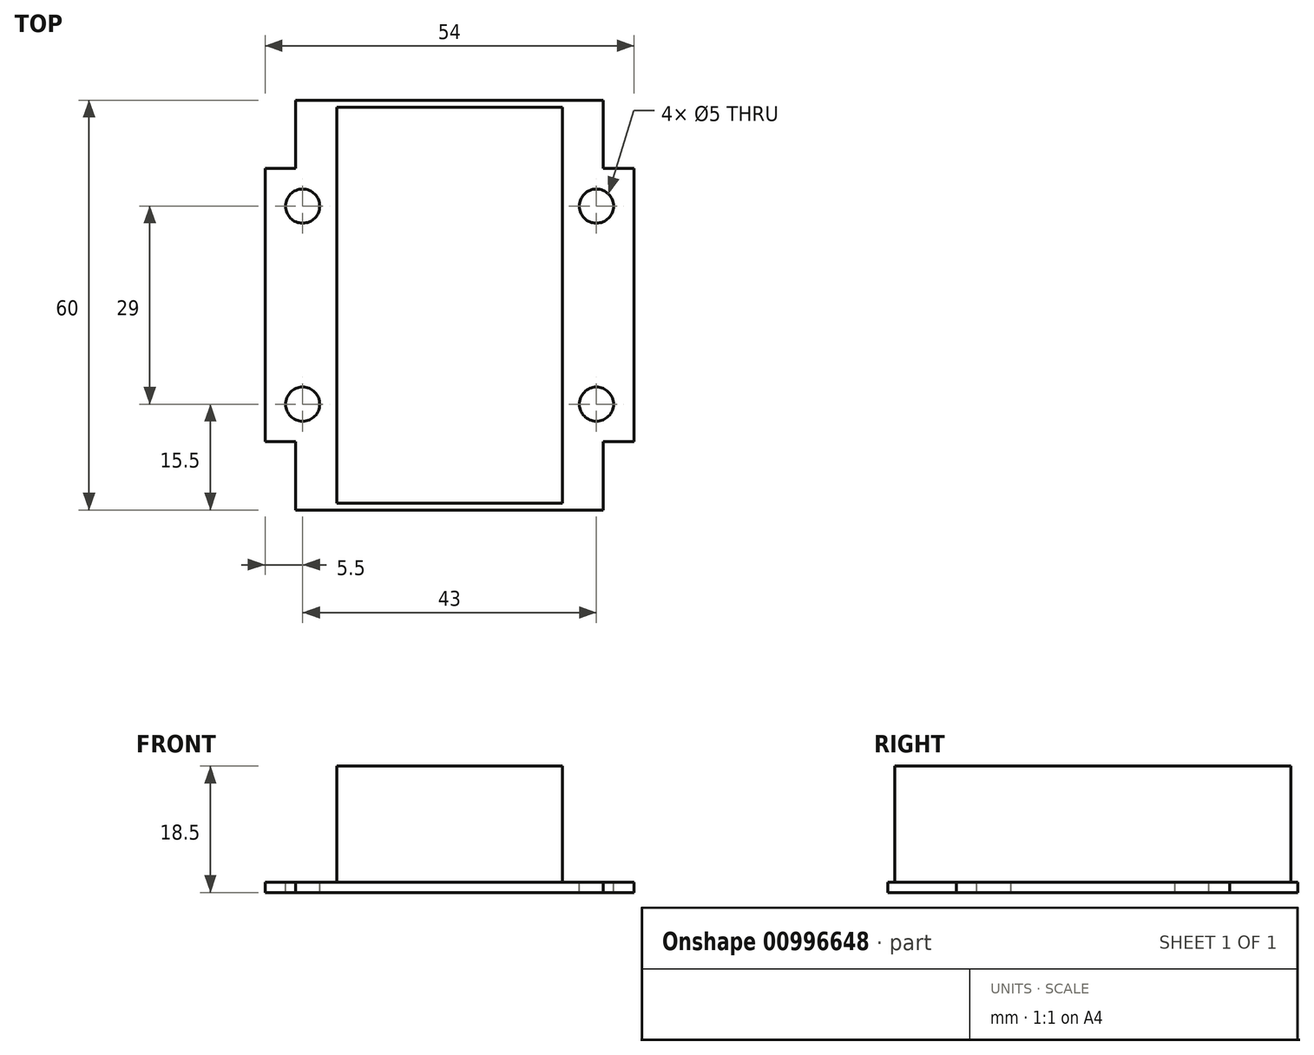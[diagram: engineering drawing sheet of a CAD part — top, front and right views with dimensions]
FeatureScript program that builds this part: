
annotation { "Feature Type Name" : "Feature", "Feature Type Description" : "" }
export const myFeature = defineFeature(function(context is Context, id is Id, definition is map)
    precondition{}
    {
        {
            var Q0;
            Q0=qCreatedBy(makeId("Top.planeOp"),FACE);
            var sketch = newSketch(context, id + "F0", { "sketchPlane" : qUnion([Q0])});
            skLineSegment(sketch, "E0.bottom", {"start": v(27, 20) * mm, "end": v(-27, 20) * mm});
            skLineSegment(sketch, "E0.top", {"start": v(27, -20) * mm, "end": v(-27, -20) * mm});
            skLineSegment(sketch, "E0.left", {"start": v(27, 20) * mm, "end": v(27, -20) * mm});
            skLineSegment(sketch, "E0.right", {"start": v(-27, 20) * mm, "end": v(-27, -20) * mm});
            skPoint(sketch, "E0.middle", {"position": v(0, 0) * mm});
            skLineSegment(sketch, "E1.bottom", {"start": v(22.5, 30) * mm, "end": v(-22.5, 30) * mm});
            skLineSegment(sketch, "E1.top", {"start": v(22.5, -30) * mm, "end": v(-22.5, -30) * mm});
            skLineSegment(sketch, "E1.left", {"start": v(22.5, 30) * mm, "end": v(22.5, -30) * mm});
            skLineSegment(sketch, "E1.right", {"start": v(-22.5, 30) * mm, "end": v(-22.5, -30) * mm});
            skSolve(sketch);
        }
        {
            var Q0;
            Q0 = qSketchRegion(id + "F0", true);
            extrude(context, id + "F1", {"entities" : qUnion([Q0]), "depth" : 1.5 * mm, "offsetDistance" : 25 * mm});
        }
        {
            var Q0;
            Q0=makeQuery(id+"F1.opExtrude","CAP_FACE",FACE,{"disambiguationData":[OSD([sQuery(id+"F0.wireOp",EDGE,"E0.bottom"),sQuery(id+"F0.wireOp",EDGE,"E0.top"),sQuery(id+"F0.wireOp",EDGE,"E0.left"),sQuery(id+"F0.wireOp",EDGE,"E0.right")])],"isStart":false});
            var sketch = newSketch(context, id + "F2", { "sketchPlane" : qUnion([Q0])});
            skLineSegment(sketch, "E2", {"start": v(-21.5, 20) * mm, "end": v(-21.5, -20) * mm, "construction": true});
            skLineSegment(sketch, "E3", {"start": v(21.5, 20) * mm, "end": v(21.5, -20) * mm, "construction": true});
            skLineSegment(sketch, "E4", {"start": v(-27, 14.5) * mm, "end": v(27, 14.5) * mm, "construction": true});
            skLineSegment(sketch, "E5", {"start": v(-27, -14.5) * mm, "end": v(27, -14.5) * mm, "construction": true});
            skCircle(sketch, "E6", {"center": v(-21.5, 14.5) * mm, "radius": 2.5 * mm});
            skCircle(sketch, "E7", {"center": v(21.5, 14.5) * mm, "radius": 2.5 * mm});
            skCircle(sketch, "E8", {"center": v(21.5, -14.5) * mm, "radius": 2.5 * mm});
            skCircle(sketch, "E9", {"center": v(-21.5, -14.5) * mm, "radius": 2.5 * mm});
            skSolve(sketch);
        }
        {
            var Q0;
            Q0 = qSketchRegion(id + "F2", true);
            extrude(context, id + "F3", {"entities" : qUnion([Q0]), "operationType" : NewBodyOperationType.REMOVE, "oppositeDirection" : true, "depth" : 25 * mm, "offsetDistance" : 25 * mm});
        }
        {
            var Q0;
            Q0=makeQuery(id+"F1.opExtrude","CAP_FACE",FACE,{"disambiguationData":[OSD([sQuery(id+"F0.wireOp",EDGE,"E0.bottom"),sQuery(id+"F0.wireOp",EDGE,"E0.top"),sQuery(id+"F0.wireOp",EDGE,"E0.left"),sQuery(id+"F0.wireOp",EDGE,"E0.right"),sQuery(id+"F0.wireOp",EDGE,"E1.bottom"),sQuery(id+"F0.wireOp",EDGE,"E1.top"),sQuery(id+"F0.wireOp",EDGE,"E1.left"),sQuery(id+"F0.wireOp",EDGE,"E1.right")])],"isStart":false});
            var sketch = newSketch(context, id + "F4", { "sketchPlane" : qUnion([Q0])});
            skLineSegment(sketch, "E10.bottom", {"start": v(16.5, 29) * mm, "end": v(-16.5, 29) * mm});
            skLineSegment(sketch, "E10.top", {"start": v(16.5, -29) * mm, "end": v(-16.5, -29) * mm});
            skLineSegment(sketch, "E10.left", {"start": v(16.5, 29) * mm, "end": v(16.5, -29) * mm});
            skLineSegment(sketch, "E10.right", {"start": v(-16.5, 29) * mm, "end": v(-16.5, -29) * mm});
            skPoint(sketch, "E10.middle", {"position": v(0, 0) * mm});
            skSolve(sketch);
        }
        {
            var Q0;
            Q0 = qSketchRegion(id + "F4", true);
            extrude(context, id + "F5", {"entities" : qUnion([Q0]), "operationType" : NewBodyOperationType.ADD, "depth" : 17 * mm, "offsetDistance" : 25 * mm});
        }
    });
